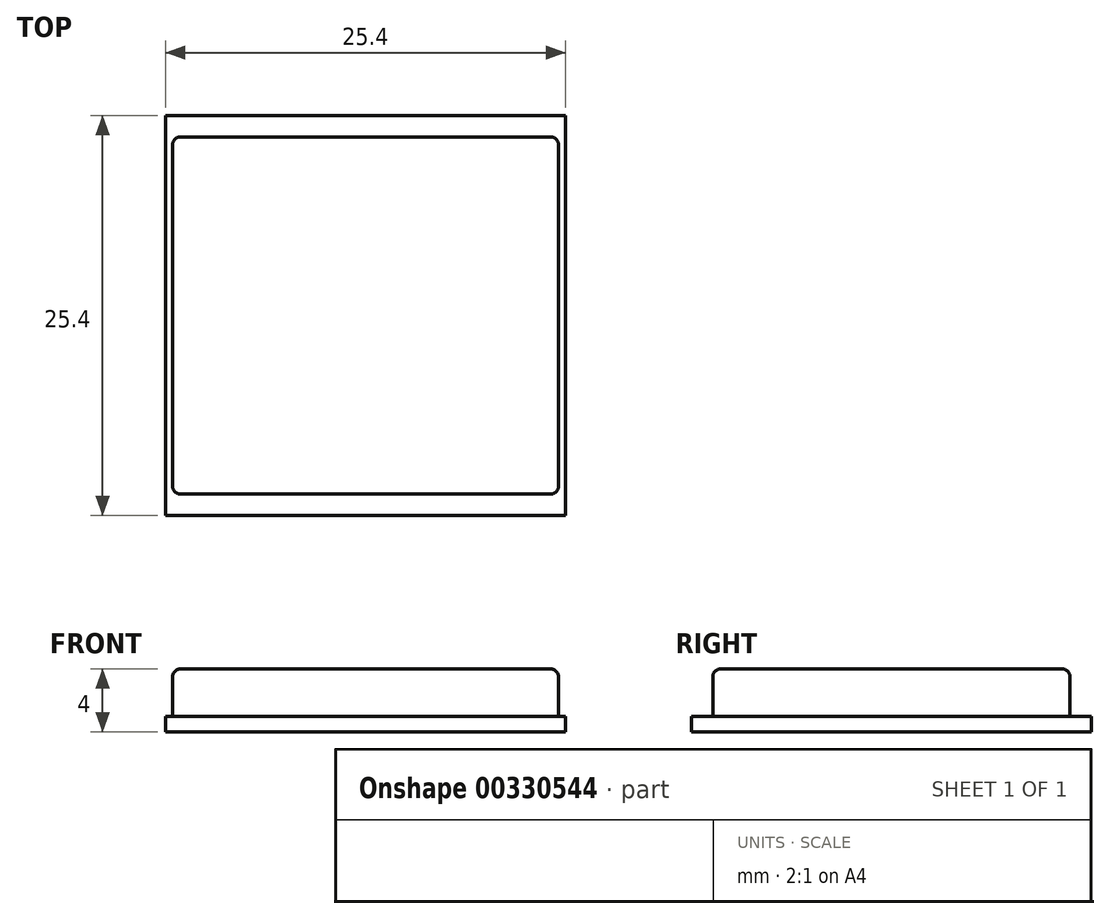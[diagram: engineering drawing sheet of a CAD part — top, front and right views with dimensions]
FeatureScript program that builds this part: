
annotation { "Feature Type Name" : "Feature", "Feature Type Description" : "" }
export const myFeature = defineFeature(function(context is Context, id is Id, definition is map)
    precondition{}
    {
        {
            var Q0;
            Q0=qCreatedBy(makeId("Top.planeOp"),FACE);
            var sketch = newSketch(context, id + "F0", { "sketchPlane" : qUnion([Q0])});
            skLineSegment(sketch, "E0.bottom", {"start": v(12.7, -12.7) * mm, "end": v(-12.7, -12.7) * mm});
            skLineSegment(sketch, "E0.top", {"start": v(12.7, 12.7) * mm, "end": v(-12.7, 12.7) * mm});
            skLineSegment(sketch, "E0.left", {"start": v(12.7, -12.7) * mm, "end": v(12.7, 12.7) * mm});
            skLineSegment(sketch, "E0.right", {"start": v(-12.7, -12.7) * mm, "end": v(-12.7, 12.7) * mm});
            skPoint(sketch, "E0.middle", {"position": v(0, 0) * mm});
            skSolve(sketch);
        }
        {
            var Q0;
            Q0 = qSketchRegion(id + "F0", true);
            extrude(context, id + "F1", {"entities" : qUnion([Q0]), "depth" : 1 * mm, "offsetDistance" : 25 * mm});
        }
        {
            var Q0;
            Q0=makeQuery(id+"F1.opExtrude","CAP_FACE",FACE,{"disambiguationData":[OSD([sQuery(id+"F0.wireOp",EDGE,"E0.bottom"),sQuery(id+"F0.wireOp",EDGE,"E0.top"),sQuery(id+"F0.wireOp",EDGE,"E0.left"),sQuery(id+"F0.wireOp",EDGE,"E0.right")])],"isStart":false});
            var sketch = newSketch(context, id + "F2", { "sketchPlane" : qUnion([Q0])});
            skLineSegment(sketch, "E1.bottom", {"start": v(12.25, -11.35) * mm, "end": v(-12.25, -11.35) * mm});
            skLineSegment(sketch, "E1.top", {"start": v(12.25, 11.35) * mm, "end": v(-12.25, 11.35) * mm});
            skLineSegment(sketch, "E1.left", {"start": v(12.25, -11.35) * mm, "end": v(12.25, 11.35) * mm});
            skLineSegment(sketch, "E1.right", {"start": v(-12.25, -11.35) * mm, "end": v(-12.25, 11.35) * mm});
            skPoint(sketch, "E1.middle", {"position": v(0, 0) * mm});
            skSolve(sketch);
        }
        {
            var Q0;
            Q0 = qSketchRegion(id + "F2", true);
            extrude(context, id + "F3", {"entities" : qUnion([Q0]), "depth" : 3 * mm, "offsetDistance" : 25 * mm});
        }
        {
            var Q0;
            Q0=makeQuery(id+"F3.opExtrude","CAP_EDGE",EDGE,{"disambiguationData":[OSD([sQuery(id+"F2.wireOp",EDGE,"E1.bottom")])],"isStart":false});
            var Q1;
            Q1=makeQuery(id+"F3.opExtrude","CAP_EDGE",EDGE,{"disambiguationData":[OSD([sQuery(id+"F2.wireOp",EDGE,"E1.left")])],"isStart":false});
            var Q2;
            Q2=makeQuery(id+"F3.opExtrude","CAP_EDGE",EDGE,{"disambiguationData":[OSD([sQuery(id+"F2.wireOp",EDGE,"E1.top")])],"isStart":false});
            var Q3;
            Q3=makeQuery(id+"F3.opExtrude","CAP_EDGE",EDGE,{"disambiguationData":[OSD([sQuery(id+"F2.wireOp",EDGE,"E1.right")])],"isStart":false});
            var Q4;
            Q4=makeQuery(id+"F3.opExtrude","SWEPT_EDGE",EDGE,{"disambiguationData":[OSD([sQuery(id+"F2.wireOp",EDGE,"E1.bottom"),sQuery(id+"F2.wireOp",EDGE,"E1.left")])]});
            var Q5;
            Q5=makeQuery(id+"F3.opExtrude","SWEPT_EDGE",EDGE,{"disambiguationData":[OSD([sQuery(id+"F2.wireOp",EDGE,"E1.bottom"),sQuery(id+"F2.wireOp",EDGE,"E1.right")])]});
            var Q6;
            Q6=makeQuery(id+"F3.opExtrude","SWEPT_EDGE",EDGE,{"disambiguationData":[OSD([sQuery(id+"F2.wireOp",EDGE,"E1.top"),sQuery(id+"F2.wireOp",EDGE,"E1.right")])]});
            var Q7;
            Q7=makeQuery(id+"F3.opExtrude","SWEPT_EDGE",EDGE,{"disambiguationData":[OSD([sQuery(id+"F2.wireOp",EDGE,"E1.top"),sQuery(id+"F2.wireOp",EDGE,"E1.left")])]});
            fillet(context, id + "F4", {"entities" : qUnion([Q0, Q1, Q2, Q3, Q4, Q5, Q6, Q7]), "radius" : .5 * mm, "tangentPropagation" : true, "allowEdgeOverflow" : false});
        }
    });
